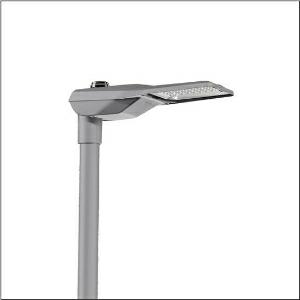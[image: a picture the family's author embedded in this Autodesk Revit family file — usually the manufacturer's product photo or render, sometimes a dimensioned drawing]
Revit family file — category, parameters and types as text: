
# Revit family: streetlight_sl_21_mini___pl52_5xe6h37n08hb_79bc
name_source: partatom
category: Lighting Fixtures
units: mm (PartAtom-declared; Revit-internal decimal feet)

## family parameters
Cut with Voids When Loaded = No
Host = Face
Light Source = No
Part Type = Normal
Room Calculation Point = No
Round Connector Dimension = Use Diameter
Shared = No

## types (1)
- --- (1 x LED, 8890 lm, 66 W, 3000K)
    Apparent Load = 66 VA
    CIE Flux Codes = 27 59 98 100 100
    Color Rendering = 70
    Color Temperature = 3000K
    Default Elevation = 1800 mm
    Description = Streetlight SL 21 mini, mast luminaire, primary light control with lens, of PMMA, primary optical cover: cover, of toughened safety glass, transparent, light distribution: PL52, light emission: direct distribution, primary light characteristic: asymmetric, installation type: side-entry, LED, 3G 1.5mm², High Power LED, rated luminous flux: 8.890lm, luminous efficacy: 135lm/W, light colour: 730, colour temperature: 3000K, control gear: NEMA (7pin), control: overheat protection, pre-setting: linear dimming characteristic, constant luminous flux control, time-dependent luminous flux control, flexible luminous flux parameterisation, mains connection: 230..240V, AC, 50/60Hz, connection cable pre-assembled, cable length: 8,5m, wiring characteristics: H07RN-F, start of lifetime: 66W, end of service life: 69W, reduction: 30W, luminaire housing, of diecast aluminium (EN AC-44300), powder-coated, SITECO metallic grey (DB 702S), corrosivity category C5 high according to DIN EN ISO 12944, multi-level sealing system, sealing non-destructively replaceable, inclination adjustable: 0°, 5°, 10°, 15°, length: 628mm, width: 235mm, height: 110mm, spigot size: 42mm (side-entry), mounting height: 4..8m, protection rating (complete): IP66, insulation class (complete): insulation class I (protective earthing), certification: CE, ENEC, ENEC+, VDE, impact resistance: IK10, permissible operating ambient temperature for outdoor applications: -40..+50°C, standard-compliant lighting for roads and squares, packaging unit: 1 piece

Light Distribution: PL52
    Height = 110 mm
    Lamp = 1 x LED
    Lamp Light Flux = 8890 lm
    Lamp Power = 66 W
    Lamp count = 1
    Length = 625 mm
    Luminous efficacy = 135 lm/W
    Manufacturer = Siteco
    ModVariant = No
    Model = 5XE6H37N08HB
    Number of Poles = 1
    OnlyDefault = Yes
    Power Factor = 1
    Product Name = Streetlight SL 21 mini | PL52
    Product group = mast luminaire | pylon top
    ProductGroupID = 6100
    Protection Class = Protection class I
    Protection Degree = IP 66
    RLX_Detail_Level = 1
    RLX_Emergency_Light_Flux = 0 lm
    RLX_Emergency_Type = 0
    RLX_Emergency_Type_DB = No
    RlxData = <blob elided: 35649 chars, md5=33cd297e>
    Socket = socket
    Standby Power = 0 W
    System Light Flux = 8890 lm
    System Power = 66 W
    Type Comments = factory setting: luminous flux: 100 % | dim-lin: 254 | 670 mA
    Type Image = l_1294379.jpg
    URL = http://relux.com
    VarID = @adj_136539
    Voltage = 0 V
    Weight = 0.00 kg
    Width = 234 mm

## geometry (parser evidence)
native form markers: Blend x4, Sweep x11
no freeform markers — native parametric forms only
